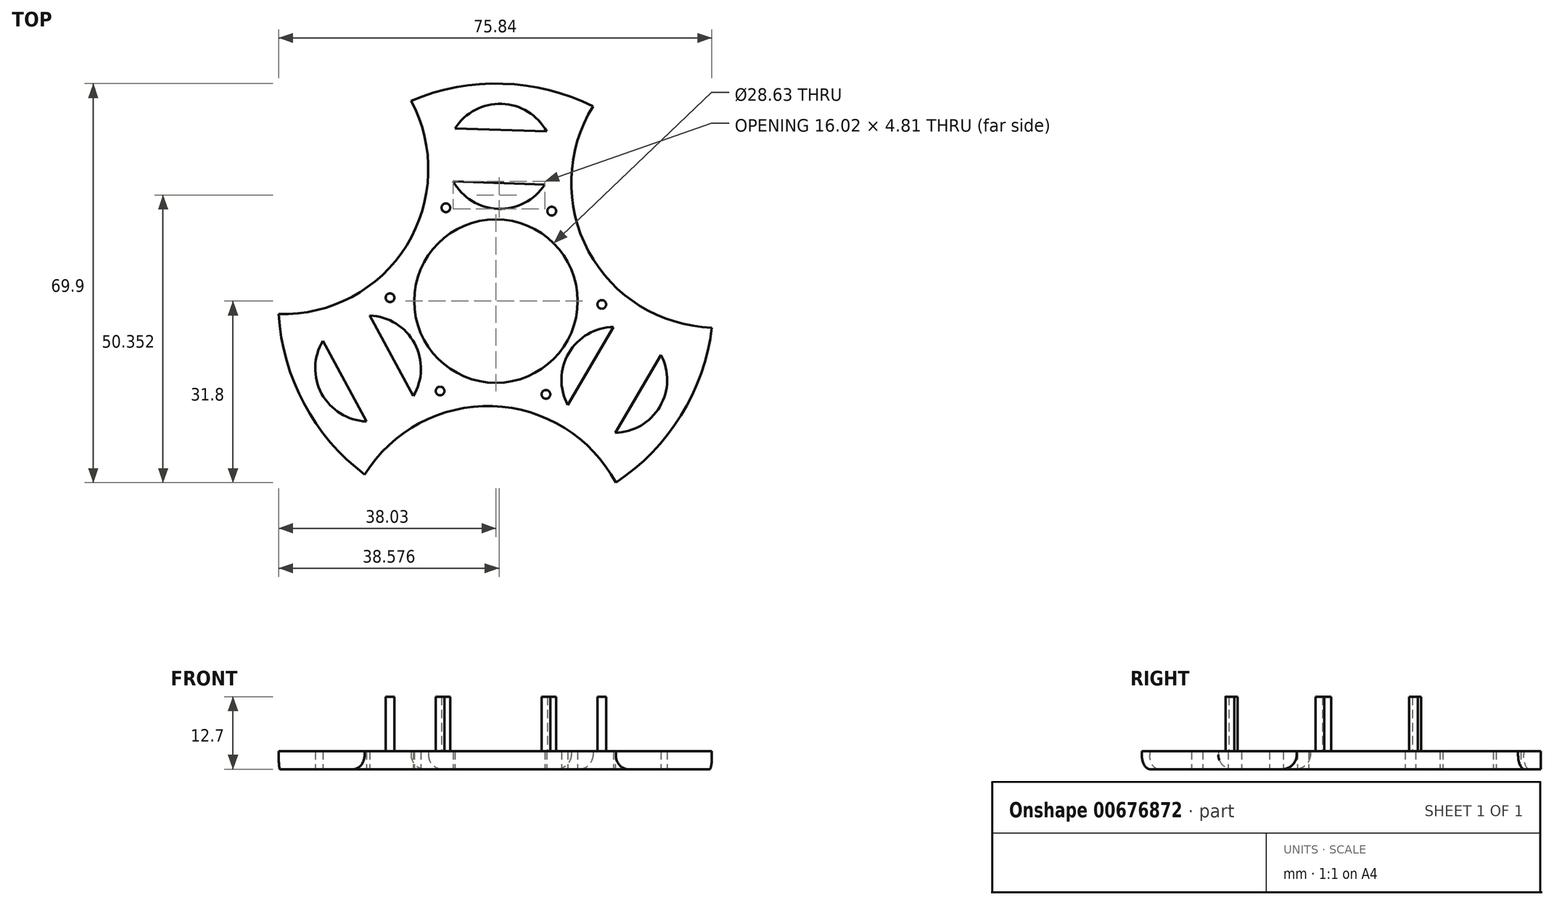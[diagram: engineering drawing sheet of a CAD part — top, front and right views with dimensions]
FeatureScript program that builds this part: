
annotation { "Feature Type Name" : "Feature", "Feature Type Description" : "" }
export const myFeature = defineFeature(function(context is Context, id is Id, definition is map)
    precondition{}
    {
        {
            var Q0;
            Q0=qCreatedBy(makeId("Top.planeOp"),FACE);
            var sketch = newSketch(context, id + "F0", { "sketchPlane" : qUnion([Q0])});
            skCircle(sketch, "E0.cCircle", {"center": v(0, 0) * mm, "radius": 38.1 * mm});
            skPoint(sketch, "E0.0.midPoint", {"position": v(-32.38, 20.08) * mm});
            skLineSegment(sketch, "E1", {"start": v(-43.96, 1.34) * mm, "end": v(20.02, 35.73) * mm, "construction": true});
            skLineSegment(sketch, "E2", {"start": v(21.09, -38.3) * mm, "end": v(20.02, 35.73) * mm, "construction": true});
            skLineSegment(sketch, "E3", {"start": v(21.09, -38.3) * mm, "end": v(-30.3, -6.99) * mm, "construction": true});
            skLineSegment(sketch, "E4", {"start": v(-20.75, 38.8) * mm, "end": v(-22.08, -2.55) * mm, "construction": true});
            skLineSegment(sketch, "E5", {"start": v(43.57, -1.57) * mm, "end": v(-23.2, -37.35) * mm, "construction": true});
            skLineSegment(sketch, "E6", {"start": v(-20.75, 38.8) * mm, "end": v(43.57, -1.57) * mm, "construction": true});
            skCircle(sketch, "E7", {"center": v(0, 0) * mm, "radius": 14.31 * mm});
            skArc(sketch, "E8", {"start": v(-38.03, -2.27) * mm, "mid": v(-15.65, 9.72) * mm, "end": v(-14.83, 35.1) * mm});
            skArc(sketch, "E9", {"start": v(17, 34.1) * mm, "mid": v(16.22, 8.71) * mm, "end": v(37.81, -4.65) * mm});
            skArc(sketch, "E10", {"start": v(21, -31.8) * mm, "mid": v(-0.59, -18.4) * mm, "end": v(-22.97, -30.4) * mm});
            skLineSegment(sketch, "E11", {"start": v(20.6, -4.54) * mm, "end": v(12.56, -18.19) * mm});
            skLineSegment(sketch, "E12", {"start": v(28.9, -9.43) * mm, "end": v(20.87, -23.08) * mm});
            skLineSegment(sketch, "E13", {"start": v(-7.46, 20.96) * mm, "end": v(8.55, 20.42) * mm});
            skLineSegment(sketch, "E14", {"start": v(-7.15, 30.27) * mm, "end": v(8.87, 29.73) * mm});
            skLineSegment(sketch, "E15", {"start": v(-30.3, -6.99) * mm, "end": v(-43.96, 1.34) * mm, "construction": true});
            skLineSegment(sketch, "E16", {"start": v(-30.3, -6.99) * mm, "end": v(-30.3, -6.99) * mm});
            skLineSegment(sketch, "E17", {"start": v(-22.08, -2.55) * mm, "end": v(-22.08, -2.55) * mm});
            skLineSegment(sketch, "E18", {"start": v(-22.08, -2.55) * mm, "end": v(-23.2, -37.35) * mm, "construction": true});
            skArc(sketch, "E19", {"start": v(-30.3, -6.99) * mm, "mid": v(-30.51, -16.21) * mm, "end": v(-22.67, -21.08) * mm});
            skArc(sketch, "E20", {"start": v(-14.46, -16.64) * mm, "mid": v(-14.25, -7.42) * mm, "end": v(-22.08, -2.55) * mm});
            skLineSegment(sketch, "E21", {"start": v(-30.3, -6.99) * mm, "end": v(-22.67, -21.08) * mm});
            skLineSegment(sketch, "E22", {"start": v(-22.08, -2.55) * mm, "end": v(-14.46, -16.64) * mm});
            skArc(sketch, "E23", {"start": v(20.6, -4.54) * mm, "mid": v(12.76, -9.1) * mm, "end": v(12.56, -18.19) * mm});
            skArc(sketch, "E24", {"start": v(20.87, -23.08) * mm, "mid": v(28.7, -18.5) * mm, "end": v(28.9, -9.43) * mm});
            skArc(sketch, "E25", {"start": v(8.87, 29.73) * mm, "mid": v(1.01, 34.56) * mm, "end": v(-7.15, 30.27) * mm});
            skArc(sketch, "E26", {"start": v(-7.46, 20.96) * mm, "mid": v(0.4, 16.15) * mm, "end": v(8.55, 20.42) * mm});
            skCircle(sketch, "E27.cCircle", {"center": v(0, 0) * mm, "radius": 16.06 * mm, "construction": true});
            skPoint(sketch, "E27.0.midPoint", {"position": v(-14.16, -7.59) * mm});
            skCircle(sketch, "E28", {"center": v(-8.76, 16.35) * mm, "radius": 0.76 * mm});
            skCircle(sketch, "E29", {"center": v(9.78, 15.76) * mm, "radius": 0.76 * mm});
            skCircle(sketch, "E30", {"center": v(18.54, -0.59) * mm, "radius": 0.76 * mm});
            skCircle(sketch, "E31", {"center": v(8.76, -16.35) * mm, "radius": 0.76 * mm});
            skCircle(sketch, "E32", {"center": v(-9.78, -15.76) * mm, "radius": 0.76 * mm});
            skCircle(sketch, "E33", {"center": v(-18.54, 0.59) * mm, "radius": 0.76 * mm});
            skSolve(sketch);
        }
        {
            var Q0;
            Q0=makeQuery(id+"F0.imprint","IMPRINT",FACE,{"disambiguationData":[TD([[makeQuery(id+"F0.imprint","IMPRINT",EDGE,{"derivedFrom":sQuery(id+"F0.wireOp",EDGE,"E7")}),-1.0]])]});
            extrude(context, id + "F1", {"entities" : qUnion([Q0]), "depth" : 3.17 * mm, "offsetDistance" : 25.4 * mm});
        }
        {
            var Q0;
            Q0=makeQuery(id+"F1.opExtrude","CAP_EDGE",EDGE,{"disambiguationData":[OSD([sQuery(id+"F0.wireOp",EDGE,"E8")])],"isStart":true});
            var Q1;
            {var subQ0=sQuery(id+"F0.wireOp",EDGE,"E0.cCircle");Q1=makeQuery(id+"F1.opExtrude","CAP_EDGE",EDGE,{"disambiguationData":[OSD([subQ0]),TDD([makeQuery(id+"F0.imprint","IMPRINT",EDGE,{"disambiguationData":[TD([[makeQuery(id+"F0.imprint","INTERSECT",VERTEX,{"disambiguationData":[OD(0.0)],"derivedFrom":[subQ0,sQuery(id+"F0.wireOp",EDGE,"E8")]}),1.0]])],"derivedFrom":subQ0})])],"isStart":true});}
            var Q2;
            Q2=makeQuery(id+"F1.opExtrude","CAP_EDGE",EDGE,{"disambiguationData":[OSD([sQuery(id+"F0.wireOp",EDGE,"E10")])],"isStart":true});
            var Q3;
            {var subQ0=sQuery(id+"F0.wireOp",EDGE,"E0.cCircle");Q3=makeQuery(id+"F1.opExtrude","CAP_EDGE",EDGE,{"disambiguationData":[OSD([subQ0]),TDD([makeQuery(id+"F0.imprint","IMPRINT",EDGE,{"disambiguationData":[TD([[makeQuery(id+"F0.imprint","INTERSECT",VERTEX,{"disambiguationData":[OD(1.0)],"derivedFrom":[subQ0,sQuery(id+"F0.wireOp",EDGE,"E9")]}),-1.0]])],"derivedFrom":subQ0})])],"isStart":true});}
            var Q4;
            Q4=makeQuery(id+"F1.opExtrude","CAP_EDGE",EDGE,{"disambiguationData":[OSD([sQuery(id+"F0.wireOp",EDGE,"E9")])],"isStart":true});
            var Q5;
            {var subQ0=sQuery(id+"F0.wireOp",EDGE,"E0.cCircle");Q5=makeQuery(id+"F1.opExtrude","CAP_EDGE",EDGE,{"disambiguationData":[OSD([subQ0]),TDD([makeQuery(id+"F0.imprint","IMPRINT",EDGE,{"disambiguationData":[TD([[makeQuery(id+"F0.imprint","INTERSECT",VERTEX,{"disambiguationData":[OD(1.0)],"derivedFrom":[subQ0,sQuery(id+"F0.wireOp",EDGE,"E8")]}),-1.0]])],"derivedFrom":subQ0})])],"isStart":true});}
            fillet(context, id + "F2", {"entities" : qUnion([Q0, Q1, Q2, Q3, Q4, Q5]), "radius" : 2.54 * mm, "tangentPropagation" : true, "allowEdgeOverflow" : false});
        }
        {
            var Q0;
            Q0=makeQuery(id+"F0.imprint","IMPRINT",FACE,{"disambiguationData":[TD([[makeQuery(id+"F0.imprint","IMPRINT",EDGE,{"derivedFrom":sQuery(id+"F0.wireOp",EDGE,"E28")}),1.0]])]});
            var Q1;
            Q1=makeQuery(id+"F0.imprint","IMPRINT",FACE,{"disambiguationData":[TD([[makeQuery(id+"F0.imprint","IMPRINT",EDGE,{"derivedFrom":sQuery(id+"F0.wireOp",EDGE,"E33")}),1.0]])]});
            var Q2;
            Q2=makeQuery(id+"F0.imprint","IMPRINT",FACE,{"disambiguationData":[TD([[makeQuery(id+"F0.imprint","IMPRINT",EDGE,{"derivedFrom":sQuery(id+"F0.wireOp",EDGE,"E32")}),1.0]])]});
            var Q3;
            Q3=makeQuery(id+"F0.imprint","IMPRINT",FACE,{"disambiguationData":[TD([[makeQuery(id+"F0.imprint","IMPRINT",EDGE,{"derivedFrom":sQuery(id+"F0.wireOp",EDGE,"E31")}),1.0]])]});
            var Q4;
            Q4=makeQuery(id+"F0.imprint","IMPRINT",FACE,{"disambiguationData":[TD([[makeQuery(id+"F0.imprint","IMPRINT",EDGE,{"derivedFrom":sQuery(id+"F0.wireOp",EDGE,"E30")}),1.0]])]});
            var Q5;
            Q5=makeQuery(id+"F0.imprint","IMPRINT",FACE,{"disambiguationData":[TD([[makeQuery(id+"F0.imprint","IMPRINT",EDGE,{"derivedFrom":sQuery(id+"F0.wireOp",EDGE,"E29")}),1.0]])]});
            extrude(context, id + "F3", {"entities" : qUnion([Q0, Q1, Q2, Q3, Q4, Q5]), "operationType" : NewBodyOperationType.ADD, "depth" : 12.7 * mm, "offsetDistance" : 25.4 * mm});
        }
    });
